# Revit family: NBS_BetafenceLimited_SStlGts_SecuriforSingleLeaf
name_source: partatom
category: Doors
revit_build: Autodesk Revit 2017 (Build: 20171027_0315(x64)
units: mm (PartAtom-declared; Revit-internal decimal feet)

## family parameters
Cut with Voids When Loaded = No
Host = Face
OmniClass Number = 23.11.25.15.17
Room Calculation Point = No
Shared = No

## types (1)
- Securifor Single Leaf
    AssetType = Fixed
    BIMObjectName = NBS_BetafenceLimited_StainlessSteelGates_SecuriforDoubleLeaf
    Category = Pr_30_59_34_80: Stainless steel gates
    CodePerformance = CE Marking
    Color = Green (RAL 6005), black (RAL 9005)
    Construction Type = HIGH_GRADE_STEEL
    Default Elevation = 0 mm  [stored 0 ft]
    Description = Swing gate
    Diameter = 0 mm  [stored 0 ft]
    DurationUnit = year
    Finish = Polyester coating
    FireExit = No
    FoundationMaterial = NBS_Concept
    Frame/MullionMaterial = NBS_Concept
    Function = Exterior
    GlazingAreaFraction = 0
    HandicapAccessible = No
    HardwareSecuring = Gate latches and catches
    Height = 2400 mm
    HeightOptions = 1000 mm, 1200 mm, 1500 mm, 1800 mm, 2000 mm, 2400 mm
    IfcExportAs = IfcDoorType
    IfcExportType = GATE
    Infiltration = 0
    IsExternal = Yes
    LeafFrameThickness = 60 mm  [stored 0.19685 ft]
    LeafMaterial = NBS_BetafenceLimited_MtlMeshPnlFncngSym_Securifor358_Panel
    LeafThickness = 60 mm  [stored 0.19685 ft]
    LowerHingeOffset = 170 mm
    ManufacturerName = Betafence Limited
    ManufacturerURL = www.betafence.co.uk
    Material = Type S235 JRH class 1, in accordance with EN 10219-1
    ModelReference = Securifor Double Leaf
    NBSCertification = www.nationalbimlibrary.com/cert/metsbjr0
    NBSDescription = Stainless steel gates
    NBSReference = 45-25-35/313
    Name = StainlessSteelGates_SecuriforDoubleLeaf_BetafenceLimited
    NominalHeight = 2400 mm
    NominalLength = 0 mm  [stored 0 ft]
    NominalWidth = 1100 mm
    Operation = DOUBLE_DOOR_SINGLE_SWING
    PostLeafGap = 40 mm  [stored 0.131234 ft]
    PostMountDepth = 750 mm  [stored 2.46063 ft]
    PostThickness = 100 mm  [stored 0.328084 ft]
    PostWidth = 100 mm  [stored 0.328084 ft]
    ProductInformation = //www.betafence.com/en/securifor-gates
    SelfClosing = No
    Size = To be taken from CAD
    SmokeStop = No
    ThermalTransmittance = 0
    Uniclass2015Code = Pr_30_59_34_80
    Uniclass2015Title = Stainless steel gates
    Uniclass2015Version = Products v1.6
    UpperHingeOffset = 180 mm
    Version = 1
    WarrantyDurationUnit = year
    Width = 1300 mm  [stored 4.26509 ft]
    WidthOptions = 2000 mm, 3000 mm, 4000 mm, 5000 mm, 6000 mm, 7000 mm, 8000 mm

note: [stored X ft] marks values corroborated as IEEE doubles in the binary element streams (Revit-internal decimal feet)

## geometry (parser evidence)
native form markers: Sweep x2
no freeform markers — native parametric forms only
